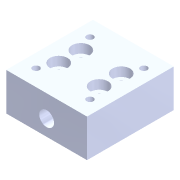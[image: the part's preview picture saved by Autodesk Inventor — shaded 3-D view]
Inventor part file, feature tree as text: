
AUTODESK INVENTOR PART (.ipt)
format: ipt  version: 2022 (Build 260153000, 153)  size: 127,488 bytes
history: mixed  units: in
note: dims shown in document units (in); Inventor stores cm internally (conversion verified against a paired STEP export)
features: hole x1, imported_body x1
ambient origin geometry x8: Origin, YZ Plane, XZ Plane, XY Plane, X Axis, Y Axis, Z Axis, Center Point
bodies: Solid1 (imported_parasolid)
feature tree (2):
  hole  "Hole2"  [1 undecoded]
  imported_body  NMx_Import_Brep_tag  [imported B-rep: ~35 faces, bbox_mm=[30.0, 14.0, 32.2]]
note: 1 required parameter value undecoded (feature->parameter linkage not recoverable at this tier; creation-order binding heuristic only, values carry confidence <= 0.55)
